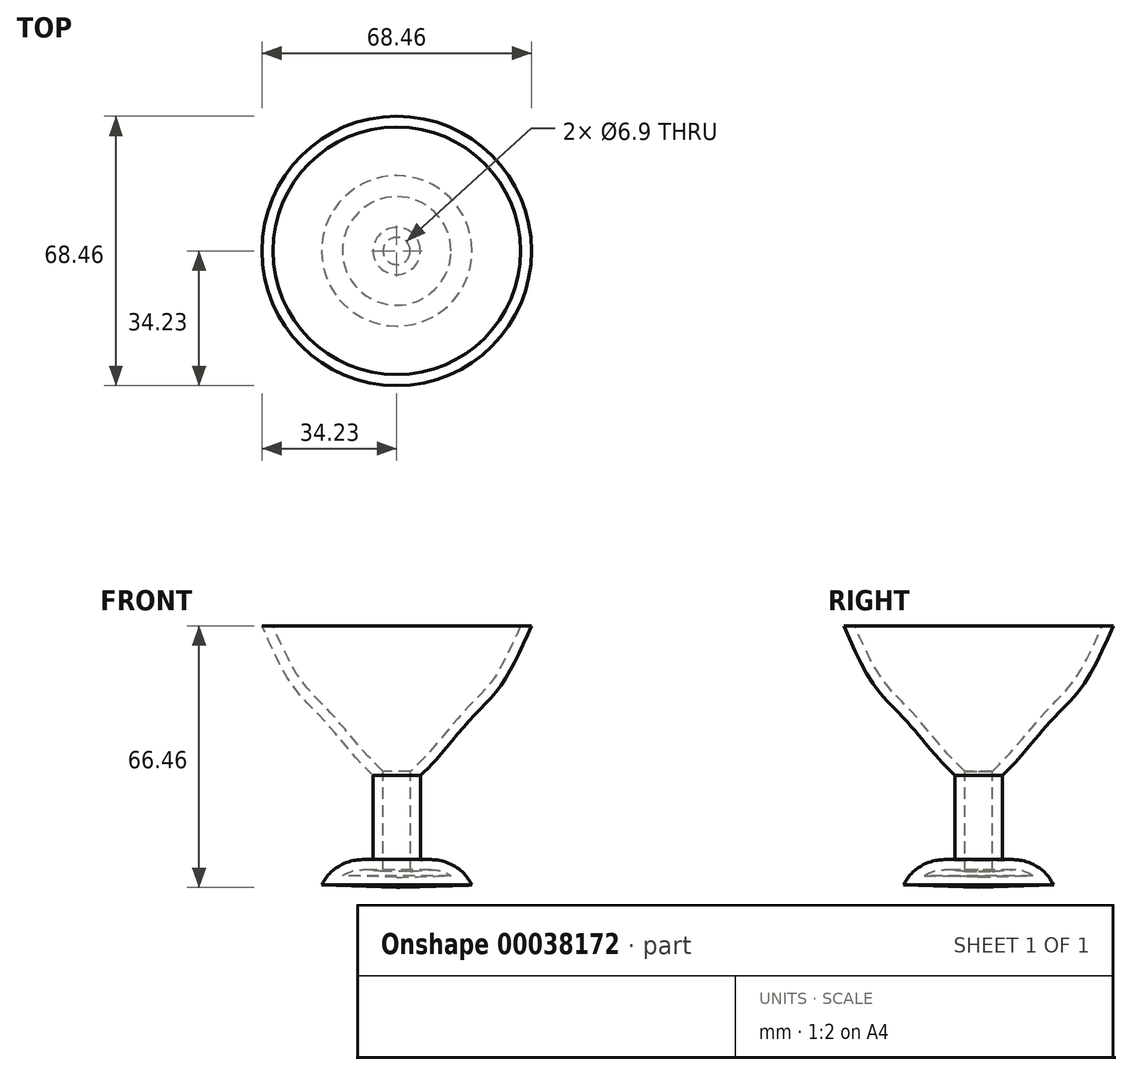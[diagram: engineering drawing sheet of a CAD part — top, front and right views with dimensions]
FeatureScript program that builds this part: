
annotation { "Feature Type Name" : "Feature", "Feature Type Description" : "" }
export const myFeature = defineFeature(function(context is Context, id is Id, definition is map)
    precondition{}
    {
        {
            var Q0;
            Q0=qCreatedBy(makeId("Front.planeOp"),FACE);
            var sketch = newSketch(context, id + "F0", { "sketchPlane" : qUnion([Q0])});
            skLineSegment(sketch, "E0", {"start": v(0, 38.08) * mm, "end": v(0, -28.38) * mm});
            skLineSegment(sketch, "E1", {"start": v(6, 0) * mm, "end": v(6, -21.54) * mm});
            skFitSpline(sketch, "E2", {"points": [v(6, -21.54) * mm, v(10.84, -21.54) * mm, v(16.26, -24.1) * mm, v(19.11, -27.81) * mm], "startDerivative": vector(14.57, 1.51) * mm, "endDerivative": vector(7.44, -12.35) * mm});
            skFitSpline(sketch, "E3", {"points": [v(19.11, -27.81) * mm, v(0, -28.38) * mm], "startDerivative": vector(-19.11, -0.57) * mm, "endDerivative": vector(-19.11, -0.57) * mm});
            skLineSegment(sketch, "E4", {"start": v(0, 38.08) * mm, "end": v(34.23, 38.08) * mm});
            skFitSpline(sketch, "E5", {"points": [v(34.23, 38.08) * mm, v(26.53, 22.96) * mm, v(18.83, 14.4) * mm, v(10.27, 4.42) * mm, v(6, 0) * mm], "startDerivative": vector(-24.16, -55.08) * mm, "endDerivative": vector(-21.58, -20.95) * mm});
            skSolve(sketch);
        }
        {
            var Q0;
            Q0=makeQuery(id+"F0.imprint","IMPRINT",FACE,{"disambiguationData":[TD([[makeQuery(id+"F0.imprint","IMPRINT",EDGE,{"derivedFrom":sQuery(id+"F0.wireOp",EDGE,"E0")}),1.0]])]});
            var Q1;
            Q1=sQuery(id+"F0.wireOp",EDGE,"E0");
            revolve(context, id + "F1", {"entities" : qUnion([Q0]), "axis" : qUnion([Q1]), "revolveType" : RevolveType.FULL});
        }
        {
            var Q0;
            Q0=makeQuery(id+"F1.opRevolve","SWEPT_FACE",FACE,{"disambiguationData":[OSD([sQuery(id+"F0.wireOp",EDGE,"E4")])]});
            shell(context, id + "F2", {"entities" : qUnion([Q0]), "thickness" : 2.54 * mm});
        }
    });
